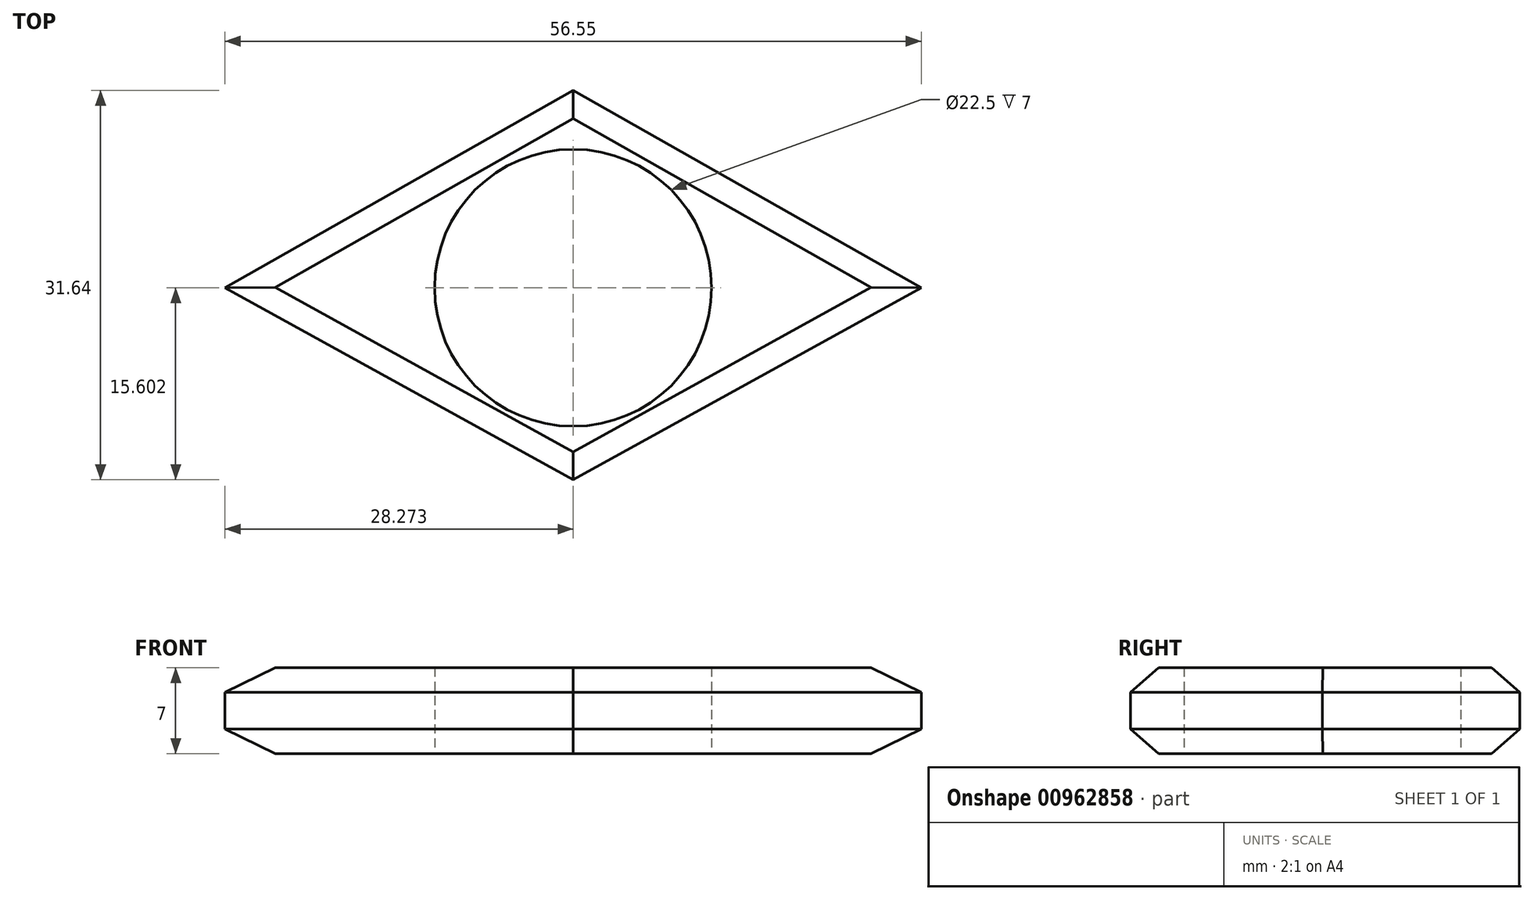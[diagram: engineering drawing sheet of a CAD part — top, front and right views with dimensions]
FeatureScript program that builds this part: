
annotation { "Feature Type Name" : "Feature", "Feature Type Description" : "" }
export const myFeature = defineFeature(function(context is Context, id is Id, definition is map)
    precondition{}
    {
        {
            var Q0;
            Q0=qCreatedBy(makeId("Top.planeOp"),FACE);
            var sketch = newSketch(context, id + "F0", { "sketchPlane" : qUnion([Q0])});
            skCircle(sketch, "E0", {"center": v(-4.73, -2.16) * mm, "radius": 11.25 * mm});
            skLineSegment(sketch, "E1", {"start": v(-4.73, 13.88) * mm, "end": v(-33, -2.16) * mm});
            skLineSegment(sketch, "E2", {"start": v(-33, -2.16) * mm, "end": v(-4.73, -17.76) * mm});
            skLineSegment(sketch, "E3", {"start": v(-4.73, -17.76) * mm, "end": v(-4.73, 13.88) * mm});
            skLineSegment(sketch, "E4.MirrorCS", {"start": v(-4.73, 13.88) * mm, "end": v(23.55, -2.16) * mm});
            skLineSegment(sketch, "E5.MirrorCS", {"start": v(23.55, -2.16) * mm, "end": v(-4.73, -17.76) * mm});
            skSolve(sketch);
        }
        {
            var Q0;
            Q0 = qSketchRegion(id + "F0", true);
            extrude(context, id + "F1", {"entities" : qUnion([Q0]), "depth" : 7 * mm, "offsetDistance" : 25 * mm});
        }
        {
            var Q0;
            Q0=makeQuery(id+"F1.opExtrude","CAP_EDGE",EDGE,{"disambiguationData":[OSD([sQuery(id+"F0.wireOp",EDGE,"E4.MirrorCS")])],"isStart":false});
            var Q1;
            Q1=makeQuery(id+"F1.opExtrude","CAP_EDGE",EDGE,{"disambiguationData":[OSD([sQuery(id+"F0.wireOp",EDGE,"E4.MirrorCS")])],"isStart":true});
            var Q2;
            Q2=makeQuery(id+"F1.opExtrude","CAP_EDGE",EDGE,{"disambiguationData":[OSD([sQuery(id+"F0.wireOp",EDGE,"E1")])],"isStart":false});
            var Q3;
            Q3=makeQuery(id+"F1.opExtrude","CAP_EDGE",EDGE,{"disambiguationData":[OSD([sQuery(id+"F0.wireOp",EDGE,"E1")])],"isStart":true});
            var Q4;
            Q4=makeQuery(id+"F1.opExtrude","CAP_EDGE",EDGE,{"disambiguationData":[OSD([sQuery(id+"F0.wireOp",EDGE,"E2")])],"isStart":false});
            var Q5;
            Q5=makeQuery(id+"F1.opExtrude","CAP_EDGE",EDGE,{"disambiguationData":[OSD([sQuery(id+"F0.wireOp",EDGE,"E2")])],"isStart":true});
            var Q6;
            Q6=makeQuery(id+"F1.opExtrude","CAP_EDGE",EDGE,{"disambiguationData":[OSD([sQuery(id+"F0.wireOp",EDGE,"E5.MirrorCS")])],"isStart":true});
            var Q7;
            Q7=makeQuery(id+"F1.opExtrude","CAP_EDGE",EDGE,{"disambiguationData":[OSD([sQuery(id+"F0.wireOp",EDGE,"E5.MirrorCS")])],"isStart":false});
            chamfer(context, id + "F2", {"entities" : qUnion([Q0, Q1, Q2, Q3, Q4, Q5, Q6, Q7]), "width" : 2 * mm, "tangentPropagation" : true});
        }
    });
